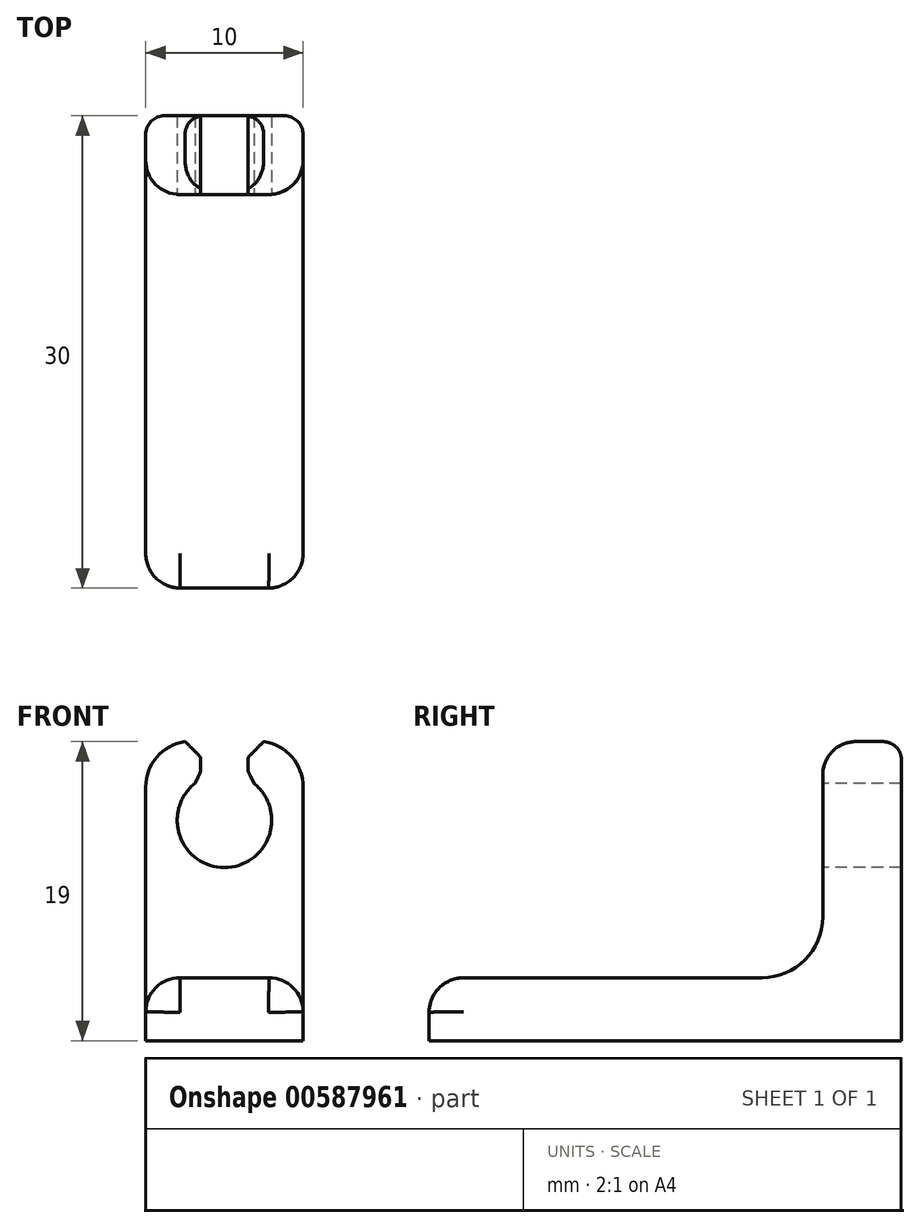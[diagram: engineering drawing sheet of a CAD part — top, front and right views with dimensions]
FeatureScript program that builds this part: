
annotation { "Feature Type Name" : "Feature", "Feature Type Description" : "" }
export const myFeature = defineFeature(function(context is Context, id is Id, definition is map)
    precondition{}
    {
        {
            var Q0;
            Q0=qCreatedBy(makeId("Right.planeOp"),FACE);
            var sketch = newSketch(context, id + "F0", { "sketchPlane" : qUnion([Q0])});
            skLineSegment(sketch, "E0.bottom", {"start": v(-13.03, 2.28) * mm, "end": v(16.97, 2.28) * mm});
            skLineSegment(sketch, "E0.top", {"start": v(-13.03, -1.72) * mm, "end": v(16.97, -1.72) * mm});
            skLineSegment(sketch, "E0.left", {"start": v(-13.03, 2.28) * mm, "end": v(-13.03, -1.72) * mm});
            skLineSegment(sketch, "E0.right", {"start": v(16.97, 2.28) * mm, "end": v(16.97, -1.72) * mm});
            skLineSegment(sketch, "E1", {"start": v(16.97, 2.28) * mm, "end": v(16.97, 17.28) * mm});
            skLineSegment(sketch, "E2", {"start": v(16.97, 17.28) * mm, "end": v(11.97, 17.28) * mm});
            skLineSegment(sketch, "E3", {"start": v(11.97, 17.28) * mm, "end": v(11.97, 2.28) * mm});
            skLineSegment(sketch, "E4", {"start": v(11.97, 2.28) * mm, "end": v(16.97, 2.28) * mm});
            skSolve(sketch);
        }
        {
            var Q0;
            Q0 = qSketchRegion(id + "F0", true);
            extrude(context, id + "F1", {"entities" : qUnion([Q0]), "depth" : 10 * mm, "offsetDistance" : 25 * mm});
        }
        {
            var Q0;
            Q0=makeQuery(id+"F1.opExtrude","SWEPT_EDGE",EDGE,{"disambiguationData":[OSD([sQuery(id+"F0.wireOp",EDGE,"E0.bottom"),sQuery(id+"F0.wireOp",EDGE,"E3"),sQuery(id+"F0.wireOp",EDGE,"E4")])]});
            fillet(context, id + "F2", {"entities" : qUnion([Q0]), "radius" : 3.86 * mm, "tangentPropagation" : true, "allowEdgeOverflow" : false});
        }
        {
            var Q0;
            Q0=makeQuery(id+"F1.opExtrude","SWEPT_FACE",FACE,{"disambiguationData":[OSD([sQuery(id+"F0.wireOp",EDGE,"E3")])]});
            var sketch = newSketch(context, id + "F3", { "sketchPlane" : qUnion([Q0])});
            skLineSegment(sketch, "E5", {"start": v(10, 6.14) * mm, "end": v(0, 6.14) * mm});
            skCircle(sketch, "E6", {"center": v(5, 12.28) * mm, "radius": 3 * mm});
            skLineSegment(sketch, "E7", {"start": v(6.5, 12.46) * mm, "end": v(6.5, 19.97) * mm});
            skPoint(sketch, "E7.startSnap0", {"position": v(6.5, 12.37) * mm});
            skLineSegment(sketch, "E8", {"start": v(3.5, 12.28) * mm, "end": v(3.5, 20.4) * mm});
            skLineSegment(sketch, "E9", {"start": v(3.5, 12.28) * mm, "end": v(6.5, 12.28) * mm});
            skLineSegment(sketch, "E10", {"start": v(6.5, 19.97) * mm, "end": v(3.5, 20.4) * mm});
            skSolve(sketch);
        }
        {
            var Q0;
            Q0 = qSketchRegion(id + "F3", true);
            extrude(context, id + "F4", {"entities" : qUnion([Q0]), "operationType" : NewBodyOperationType.REMOVE, "oppositeDirection" : true, "depth" : 25 * mm, "offsetDistance" : 25 * mm});
        }
        {
            var Q0;
            Q0=makeQuery(id+"F4.boolean.opBoolean","INTERSECT",EDGE,{"derivedFrom":[makeQuery(id+"F1.opExtrude","SWEPT_FACE",FACE,{"disambiguationData":[OSD([sQuery(id+"F0.wireOp",EDGE,"E2")])]}),makeQuery(id+"F4.opExtrude","SWEPT_FACE",FACE,{"disambiguationData":[OSD([sQuery(id+"F3.wireOp",EDGE,"E8")])]})]});
            var Q1;
            Q1=makeQuery(id+"F4.boolean.opBoolean","INTERSECT",EDGE,{"derivedFrom":[makeQuery(id+"F1.opExtrude","SWEPT_FACE",FACE,{"disambiguationData":[OSD([sQuery(id+"F0.wireOp",EDGE,"E2")])]}),makeQuery(id+"F4.opExtrude","SWEPT_FACE",FACE,{"disambiguationData":[OSD([sQuery(id+"F3.wireOp",EDGE,"E7")])]})]});
            var Q2;
            Q2=makeQuery(id+"F4.boolean.opBoolean","COPY",EDGE,{"derivedFrom":makeQuery(id+"F4.opExtrude","SWEPT_EDGE",EDGE,{"disambiguationData":[OSD([sQuery(id+"F3.wireOp",EDGE,"E6"),sQuery(id+"F3.wireOp",EDGE,"E8")])]})});
            var Q3;
            Q3=makeQuery(id+"F4.boolean.opBoolean","COPY",EDGE,{"derivedFrom":makeQuery(id+"F4.opExtrude","SWEPT_EDGE",EDGE,{"disambiguationData":[OSD([sQuery(id+"F3.wireOp",EDGE,"E6"),sQuery(id+"F3.wireOp",EDGE,"E7")])]})});
            chamfer(context, id + "F5", {"entities" : qUnion([Q0, Q1, Q2, Q3]), "width" : 1 * mm, "tangentPropagation" : true});
        }
        {
            var Q0;
            {var subQ0=makeQuery(id+"F4.opExtrude","SWEPT_FACE",FACE,{"disambiguationData":[OSD([sQuery(id+"F3.wireOp",EDGE,"E8")])]});Q0=makeQuery(id+"F5.opChamfer","BLEND_EDGE",EDGE,{"blendedFrom":[makeQuery(id+"F4.boolean.opBoolean","INTERSECT",EDGE,{"derivedFrom":[makeQuery(id+"F1.opExtrude","SWEPT_FACE",FACE,{"disambiguationData":[OSD([sQuery(id+"F0.wireOp",EDGE,"E2")])]}),subQ0]}),makeQuery(id+"F4.boolean.opBoolean","COPY",FACE,{"derivedFrom":subQ0})],"blendedInto":[makeQuery(id+"F4.boolean.opBoolean","COPY",FACE,{"derivedFrom":subQ0})]});}
            var Q1;
            {var subQ0=sQuery(id+"F3.wireOp",EDGE,"E8");Q1=makeQuery(id+"F5.opChamfer","BLEND_EDGE",EDGE,{"blendedFrom":[makeQuery(id+"F4.boolean.opBoolean","COPY",EDGE,{"derivedFrom":makeQuery(id+"F4.opExtrude","SWEPT_EDGE",EDGE,{"disambiguationData":[OSD([sQuery(id+"F3.wireOp",EDGE,"E6"),subQ0])]})}),makeQuery(id+"F4.boolean.opBoolean","COPY",FACE,{"derivedFrom":makeQuery(id+"F4.opExtrude","SWEPT_FACE",FACE,{"disambiguationData":[OSD([subQ0])]})})],"blendedInto":[makeQuery(id+"F4.boolean.opBoolean","COPY",FACE,{"derivedFrom":makeQuery(id+"F4.opExtrude","SWEPT_FACE",FACE,{"disambiguationData":[OSD([subQ0])]})})]});}
            var Q2;
            {var subQ0=makeQuery(id+"F4.opExtrude","SWEPT_FACE",FACE,{"disambiguationData":[OSD([sQuery(id+"F3.wireOp",EDGE,"E7")])]});Q2=makeQuery(id+"F5.opChamfer","BLEND_EDGE",EDGE,{"blendedFrom":[makeQuery(id+"F4.boolean.opBoolean","INTERSECT",EDGE,{"derivedFrom":[makeQuery(id+"F1.opExtrude","SWEPT_FACE",FACE,{"disambiguationData":[OSD([sQuery(id+"F0.wireOp",EDGE,"E2")])]}),subQ0]}),makeQuery(id+"F4.boolean.opBoolean","COPY",FACE,{"derivedFrom":subQ0})],"blendedInto":[makeQuery(id+"F4.boolean.opBoolean","COPY",FACE,{"derivedFrom":subQ0})]});}
            var Q3;
            {var subQ0=sQuery(id+"F3.wireOp",EDGE,"E7");Q3=makeQuery(id+"F5.opChamfer","BLEND_EDGE",EDGE,{"blendedFrom":[makeQuery(id+"F4.boolean.opBoolean","COPY",EDGE,{"derivedFrom":makeQuery(id+"F4.opExtrude","SWEPT_EDGE",EDGE,{"disambiguationData":[OSD([sQuery(id+"F3.wireOp",EDGE,"E6"),subQ0])]})}),makeQuery(id+"F4.boolean.opBoolean","COPY",FACE,{"derivedFrom":makeQuery(id+"F4.opExtrude","SWEPT_FACE",FACE,{"disambiguationData":[OSD([subQ0])]})})],"blendedInto":[makeQuery(id+"F4.boolean.opBoolean","COPY",FACE,{"derivedFrom":makeQuery(id+"F4.opExtrude","SWEPT_FACE",FACE,{"disambiguationData":[OSD([subQ0])]})})]});}
            fillet(context, id + "F6", {"entities" : qUnion([Q0, Q1, Q2, Q3]), "radius" : 0.39 * mm, "tangentPropagation" : true, "allowEdgeOverflow" : false});
        }
        {
            var Q0;
            Q0=makeQuery(id+"F1.opExtrude","CAP_EDGE",EDGE,{"disambiguationData":[OSD([sQuery(id+"F0.wireOp",EDGE,"E2")])],"isStart":false});
            var Q1;
            Q1=makeQuery(id+"F1.opExtrude","CAP_EDGE",EDGE,{"disambiguationData":[OSD([sQuery(id+"F0.wireOp",EDGE,"E2")])],"isStart":true});
            fillet(context, id + "F7", {"entities" : qUnion([Q0, Q1]), "radius" : 2.92 * mm, "tangentPropagation" : true, "allowEdgeOverflow" : false});
        }
        {
            var Q0;
            Q0=makeQuery(id+"F1.opExtrude","CAP_EDGE",EDGE,{"disambiguationData":[OSD([sQuery(id+"F0.wireOp",EDGE,"E0.bottom")])],"isStart":false});
            var Q1;
            {var subQ0=sQuery(id+"F0.wireOp",EDGE,"E3");var subQ1=sQuery(id+"F0.wireOp",EDGE,"E0.bottom");Q1=makeQuery(id+"F2.opFillet","BLEND_EDGE",EDGE,{"blendedFrom":[makeQuery(id+"F1.opExtrude","SWEPT_EDGE",EDGE,{"disambiguationData":[OSD([subQ1,subQ0,sQuery(id+"F0.wireOp",EDGE,"E4")])]}),makeQuery(id+"F1.opExtrude","CAP_FACE",FACE,{"disambiguationData":[OSD([subQ1,sQuery(id+"F0.wireOp",EDGE,"E0.top"),sQuery(id+"F0.wireOp",EDGE,"E0.left"),sQuery(id+"F0.wireOp",EDGE,"E0.right"),sQuery(id+"F0.wireOp",EDGE,"E1"),sQuery(id+"F0.wireOp",EDGE,"E2"),subQ0])],"isStart":false})],"blendedInto":[makeQuery(id+"F1.opExtrude","CAP_FACE",FACE,{"disambiguationData":[OSD([subQ1,sQuery(id+"F0.wireOp",EDGE,"E0.top"),sQuery(id+"F0.wireOp",EDGE,"E0.left"),sQuery(id+"F0.wireOp",EDGE,"E0.right"),sQuery(id+"F0.wireOp",EDGE,"E1"),sQuery(id+"F0.wireOp",EDGE,"E2"),subQ0])],"isStart":false})]});}
            var Q2;
            {var subQ0=sQuery(id+"F0.wireOp",EDGE,"E3");var subQ1=sQuery(id+"F0.wireOp",EDGE,"E0.bottom");Q2=makeQuery(id+"F2.opFillet","BLEND_EDGE",EDGE,{"blendedFrom":[makeQuery(id+"F1.opExtrude","SWEPT_EDGE",EDGE,{"disambiguationData":[OSD([subQ1,subQ0,sQuery(id+"F0.wireOp",EDGE,"E4")])]}),makeQuery(id+"F1.opExtrude","CAP_FACE",FACE,{"disambiguationData":[OSD([subQ1,sQuery(id+"F0.wireOp",EDGE,"E0.top"),sQuery(id+"F0.wireOp",EDGE,"E0.left"),sQuery(id+"F0.wireOp",EDGE,"E0.right"),sQuery(id+"F0.wireOp",EDGE,"E1"),sQuery(id+"F0.wireOp",EDGE,"E2"),subQ0])],"isStart":true})],"blendedInto":[makeQuery(id+"F1.opExtrude","CAP_FACE",FACE,{"disambiguationData":[OSD([subQ1,sQuery(id+"F0.wireOp",EDGE,"E0.top"),sQuery(id+"F0.wireOp",EDGE,"E0.left"),sQuery(id+"F0.wireOp",EDGE,"E0.right"),sQuery(id+"F0.wireOp",EDGE,"E1"),sQuery(id+"F0.wireOp",EDGE,"E2"),subQ0])],"isStart":true})]});}
            var Q3;
            Q3=makeQuery(id+"F1.opExtrude","CAP_EDGE",EDGE,{"disambiguationData":[OSD([sQuery(id+"F0.wireOp",EDGE,"E0.bottom")])],"isStart":true});
            fillet(context, id + "F8", {"entities" : qUnion([Q0, Q1, Q2, Q3]), "radius" : 2.17 * mm, "tangentPropagation" : true, "allowEdgeOverflow" : false});
        }
        {
            var Q0;
            Q0=makeQuery(id+"F1.opExtrude","CAP_EDGE",EDGE,{"disambiguationData":[OSD([sQuery(id+"F0.wireOp",EDGE,"E0.right"),sQuery(id+"F0.wireOp",EDGE,"E1")])],"isStart":false});
            var Q1;
            Q1=makeQuery(id+"F1.opExtrude","CAP_EDGE",EDGE,{"disambiguationData":[OSD([sQuery(id+"F0.wireOp",EDGE,"E0.right"),sQuery(id+"F0.wireOp",EDGE,"E1")])],"isStart":true});
            fillet(context, id + "F9", {"entities" : qUnion([Q0, Q1]), "radius" : 1.2 * mm, "tangentPropagation" : true, "allowEdgeOverflow" : false});
        }
        {
            var Q0;
            Q0=makeQuery(id+"F1.opExtrude","SWEPT_EDGE",EDGE,{"disambiguationData":[OSD([sQuery(id+"F0.wireOp",EDGE,"E0.bottom"),sQuery(id+"F0.wireOp",EDGE,"E0.left")])]});
            var Q1;
            Q1=makeQuery(id+"F8.opFillet","BLEND_EDGE",EDGE,{"blendedFrom":[makeQuery(id+"F1.opExtrude","CAP_EDGE",EDGE,{"disambiguationData":[OSD([sQuery(id+"F0.wireOp",EDGE,"E0.bottom")])],"isStart":true}),makeQuery(id+"F1.opExtrude","SWEPT_FACE",FACE,{"disambiguationData":[OSD([sQuery(id+"F0.wireOp",EDGE,"E0.left")])]})],"blendedInto":[makeQuery(id+"F1.opExtrude","SWEPT_FACE",FACE,{"disambiguationData":[OSD([sQuery(id+"F0.wireOp",EDGE,"E0.left")])]})]});
            var Q2;
            Q2=makeQuery(id+"F1.opExtrude","CAP_EDGE",EDGE,{"disambiguationData":[OSD([sQuery(id+"F0.wireOp",EDGE,"E0.left")])],"isStart":true});
            var Q3;
            Q3=makeQuery(id+"F8.opFillet","BLEND_EDGE",EDGE,{"blendedFrom":[makeQuery(id+"F1.opExtrude","CAP_EDGE",EDGE,{"disambiguationData":[OSD([sQuery(id+"F0.wireOp",EDGE,"E0.bottom")])],"isStart":false}),makeQuery(id+"F1.opExtrude","SWEPT_FACE",FACE,{"disambiguationData":[OSD([sQuery(id+"F0.wireOp",EDGE,"E0.left")])]})],"blendedInto":[makeQuery(id+"F1.opExtrude","SWEPT_FACE",FACE,{"disambiguationData":[OSD([sQuery(id+"F0.wireOp",EDGE,"E0.left")])]})]});
            var Q4;
            Q4=makeQuery(id+"F1.opExtrude","CAP_EDGE",EDGE,{"disambiguationData":[OSD([sQuery(id+"F0.wireOp",EDGE,"E0.left")])],"isStart":false});
            fillet(context, id + "F10", {"entities" : qUnion([Q0, Q1, Q2, Q3, Q4]), "radius" : 2.2 * mm, "tangentPropagation" : true, "allowEdgeOverflow" : false});
        }
    });
